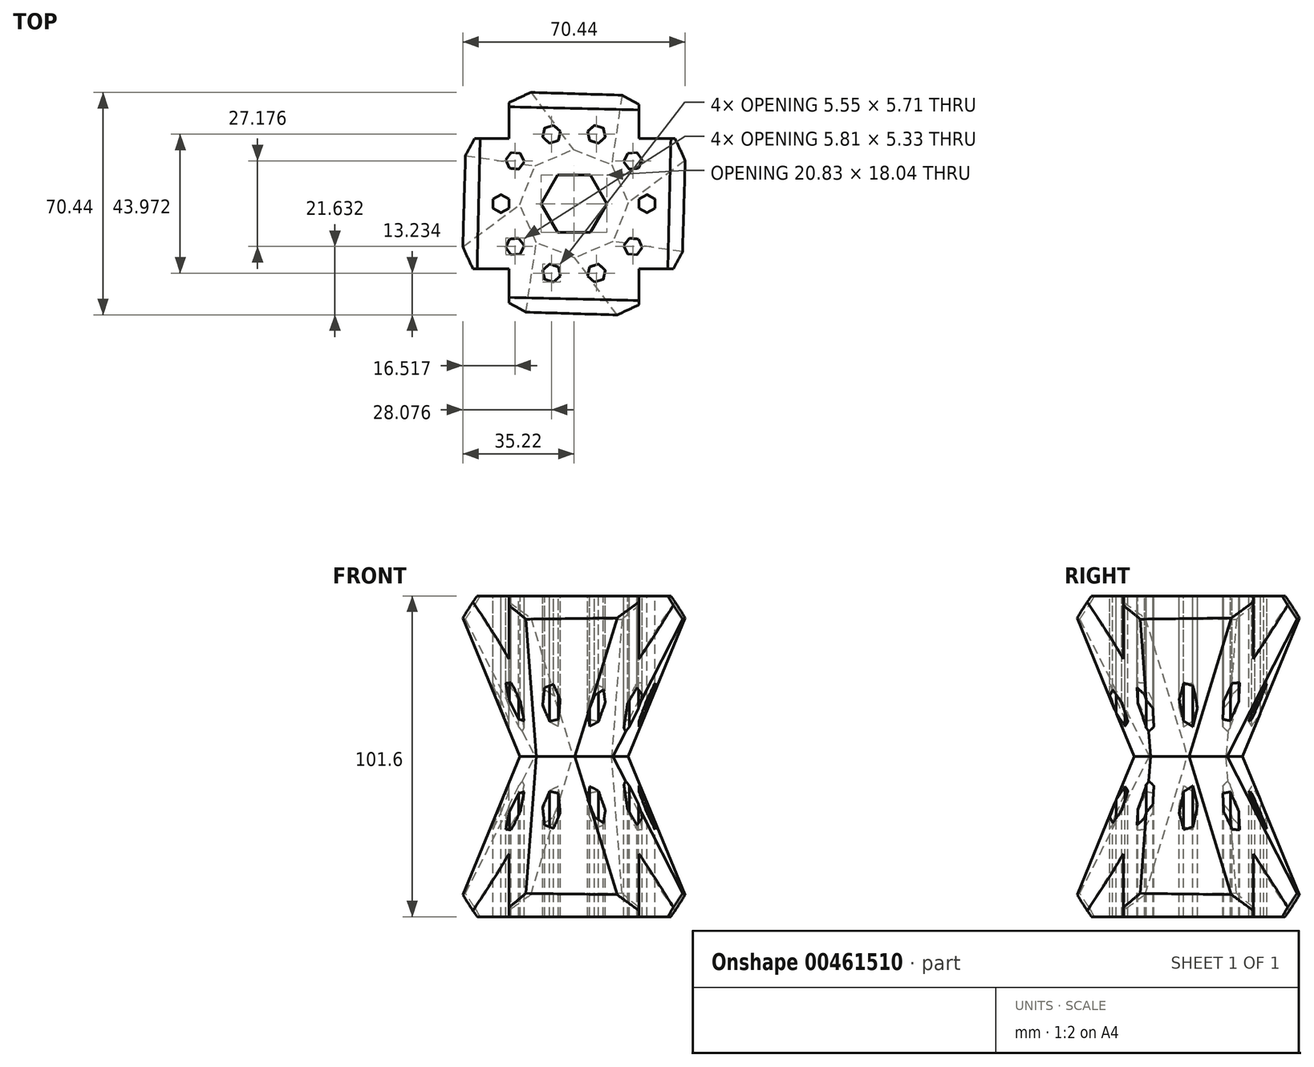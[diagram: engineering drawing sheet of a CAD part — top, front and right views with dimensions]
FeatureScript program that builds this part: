
annotation { "Feature Type Name" : "Feature", "Feature Type Description" : "" }
export const myFeature = defineFeature(function(context is Context, id is Id, definition is map)
    precondition{}
    {
        {
            var Q0;
            Q0=qCreatedBy(makeId("Top.planeOp"),FACE);
            var sketch = newSketch(context, id + "F0", { "sketchPlane" : qUnion([Q0])});
            skLineSegment(sketch, "E0", {"start": v(-123.7, 48.81) * mm, "end": v(88.1, 48.81) * mm, "construction": true});
            skCircle(sketch, "E1.cCircle", {"center": v(0, 0) * mm, "radius": 38.1 * mm, "construction": true});
            skLineSegment(sketch, "E1.0", {"start": v(15.78, 38.1) * mm, "end": v(38.1, 15.78) * mm});
            skLineSegment(sketch, "E1.1", {"start": v(38.1, 15.78) * mm, "end": v(38.1, -15.78) * mm});
            skLineSegment(sketch, "E1.2", {"start": v(38.1, -15.78) * mm, "end": v(15.78, -38.1) * mm});
            skLineSegment(sketch, "E1.3", {"start": v(15.78, -38.1) * mm, "end": v(-15.78, -38.1) * mm});
            skLineSegment(sketch, "E1.4", {"start": v(-15.78, -38.1) * mm, "end": v(-38.1, -15.78) * mm});
            skLineSegment(sketch, "E1.5", {"start": v(-38.1, -15.78) * mm, "end": v(-38.1, 15.78) * mm});
            skLineSegment(sketch, "E1.6", {"start": v(-38.1, 15.78) * mm, "end": v(-15.78, 38.1) * mm});
            skLineSegment(sketch, "E1.7", {"start": v(-15.78, 38.1) * mm, "end": v(15.78, 38.1) * mm});
            skPoint(sketch, "E1.0.midPoint", {"position": v(26.94, 26.94) * mm});
            skSolve(sketch);
        }
        {
            var Q0;
            Q0=qCreatedBy(makeId("Top.planeOp"),FACE);
            cPlane(context, id + "F1", {"entities" : qUnion([Q0]), "cplaneType" : CPlaneType.OFFSET, "offset" : 50.8 * mm, "width" : 152.4 * mm, "height" : 152.4 * mm});
        }
        {
            var Q0;
            Q0=qCreatedBy(id+"F1.planeOp",FACE);
            var sketch = newSketch(context, id + "F2", { "sketchPlane" : qUnion([Q0])});
            skCircle(sketch, "E2.cCircle", {"center": v(0, 0) * mm, "radius": 15.88 * mm, "construction": true});
            skLineSegment(sketch, "E2.0", {"start": v(0.3, -17.18) * mm, "end": v(-11.94, -12.36) * mm});
            skLineSegment(sketch, "E2.1", {"start": v(-11.94, -12.36) * mm, "end": v(-17.18, -0.3) * mm});
            skLineSegment(sketch, "E2.2", {"start": v(-17.18, -0.3) * mm, "end": v(-12.36, 11.94) * mm});
            skLineSegment(sketch, "E2.3", {"start": v(-12.36, 11.94) * mm, "end": v(-0.3, 17.18) * mm});
            skLineSegment(sketch, "E2.4", {"start": v(-0.3, 17.18) * mm, "end": v(11.94, 12.36) * mm});
            skLineSegment(sketch, "E2.5", {"start": v(11.94, 12.36) * mm, "end": v(17.18, 0.3) * mm});
            skLineSegment(sketch, "E2.6", {"start": v(17.18, 0.3) * mm, "end": v(12.36, -11.94) * mm});
            skLineSegment(sketch, "E2.7", {"start": v(12.36, -11.94) * mm, "end": v(0.3, -17.18) * mm});
            skPoint(sketch, "E2.0.midPoint", {"position": v(-5.82, -14.77) * mm});
            skSolve(sketch);
        }
        {
            var Q0;
            Q0=makeQuery(id+"F0.imprint","IMPRINT",FACE,{"disambiguationData":[TD([[makeQuery(id+"F0.imprint","IMPRINT",EDGE,{"derivedFrom":sQuery(id+"F0.wireOp",EDGE,"E1.0")}),-1.0]])]});
            var Q1;
            Q1=makeQuery(id+"F2.imprint","IMPRINT",FACE,{"disambiguationData":[TD([[makeQuery(id+"F2.imprint","IMPRINT",EDGE,{"derivedFrom":sQuery(id+"F2.wireOp",EDGE,"E2.0")}),-1.0]])]});
            loft(context, id + "F3", {"sheetProfilesArray" : [{ "sheetProfileEntities" : qUnion([Q0]) }, { "sheetProfileEntities" : qUnion([Q1]) }]});
        }
        {
            var Q0;
            Q0=makeQuery(id+"F3.opLoft","SWEPT_BODY",BODY,{"disambiguationData":[OSD([makeQuery(id+"F0.imprint","IMPRINT",FACE,{"disambiguationData":[TD([[makeQuery(id+"F0.imprint","IMPRINT",EDGE,{"derivedFrom":sQuery(id+"F0.wireOp",EDGE,"E1.0")}),-1.0]])]}),makeQuery(id+"F2.imprint","IMPRINT",FACE,{"disambiguationData":[TD([[makeQuery(id+"F2.imprint","IMPRINT",EDGE,{"derivedFrom":sQuery(id+"F2.wireOp",EDGE,"E2.0")}),-1.0]])]})])]});
            var Q1;
            Q1=qCreatedBy(id+"F1.planeOp",FACE);
            mirror(context, id + "F4", {"operationType" : NewBodyOperationType.ADD, "entities" : qUnion([Q0]), "mirrorPlane" : qUnion([Q1])});
        }
        {
            var Q0;
            Q0=makeQuery(id+"F4.opPattern","COPY",FACE,{"derivedFrom":makeQuery(id+"F3.opLoft","CAP_FACE",FACE,{"disambiguationData":[OSD([makeQuery(id+"F0.imprint","IMPRINT",FACE,{"disambiguationData":[TD([[makeQuery(id+"F0.imprint","IMPRINT",EDGE,{"derivedFrom":sQuery(id+"F0.wireOp",EDGE,"E1.0")}),-1.0]])]})])],"isStart":true}),"instanceName":"1"});
            var sketch = newSketch(context, id + "F5", { "sketchPlane" : qUnion([Q0])});
            skLineSegment(sketch, "E3", {"start": v(0, -25.16) * mm, "end": v(0, 28.29) * mm, "construction": true});
            skCircle(sketch, "E4.cCircle", {"center": v(0, 0) * mm, "radius": 9.02 * mm, "construction": true});
            skLineSegment(sketch, "E4.0", {"start": v(-10.41, 0) * mm, "end": v(-5.2, 9.02) * mm});
            skLineSegment(sketch, "E4.1", {"start": v(-5.2, 9.02) * mm, "end": v(5.2, 9.02) * mm});
            skLineSegment(sketch, "E4.2", {"start": v(5.2, 9.02) * mm, "end": v(10.41, 0) * mm});
            skLineSegment(sketch, "E4.3", {"start": v(10.41, 0) * mm, "end": v(5.2, -9.02) * mm});
            skLineSegment(sketch, "E4.4", {"start": v(5.2, -9.02) * mm, "end": v(-5.2, -9.02) * mm});
            skLineSegment(sketch, "E4.5", {"start": v(-5.2, -9.02) * mm, "end": v(-10.41, 0) * mm});
            skPoint(sketch, "E4.0.midPoint", {"position": v(-7.81, 4.5) * mm});
            skSolve(sketch);
        }
        {
            var Q0;
            Q0=makeQuery(id+"F5.imprint","IMPRINT",FACE,{"disambiguationData":[TD([[makeQuery(id+"F5.imprint","IMPRINT",EDGE,{"derivedFrom":sQuery(id+"F5.wireOp",EDGE,"E4.0")}),-1.0]])]});
            extrude(context, id + "F6", {"entities" : qUnion([Q0]), "operationType" : NewBodyOperationType.REMOVE, "endBound" : BoundingType.THROUGH_ALL, "oppositeDirection" : true, "depth" : 25.4 * mm});
        }
        {
            var Q0;
            Q0=makeQuery(id+"F4.opPattern","COPY",FACE,{"derivedFrom":makeQuery(id+"F3.opLoft","CAP_FACE",FACE,{"disambiguationData":[OSD([makeQuery(id+"F0.imprint","IMPRINT",FACE,{"disambiguationData":[TD([[makeQuery(id+"F0.imprint","IMPRINT",EDGE,{"derivedFrom":sQuery(id+"F0.wireOp",EDGE,"E1.0")}),-1.0]])]})])],"isStart":true}),"instanceName":"1"});
            var sketch = newSketch(context, id + "F7", { "sketchPlane" : qUnion([Q0])});
            skLineSegment(sketch, "E5", {"start": v(20.6, -33.3) * mm, "end": v(20.6, -20.6) * mm});
            skLineSegment(sketch, "E6", {"start": v(20.6, -20.6) * mm, "end": v(33.3, -20.6) * mm});
            skLineSegment(sketch, "E7", {"start": v(20.6, -20.6) * mm, "end": v(26.94, -26.94) * mm, "construction": true});
            skLineSegment(sketch, "E8.0", {"start": v(15.78, -38.1) * mm, "end": v(38.1, -15.78) * mm, "construction": true});
            skLineSegment(sketch, "E9", {"start": v(33.3, -20.6) * mm, "end": v(20.6, -33.3) * mm});
            skLineSegment(sketch, "E10.1.0", {"start": v(33.3, 20.6) * mm, "end": v(20.6, 20.6) * mm});
            skLineSegment(sketch, "E10.1.1", {"start": v(20.6, 20.6) * mm, "end": v(20.6, 33.3) * mm});
            skLineSegment(sketch, "E10.1.2", {"start": v(38.1, 15.78) * mm, "end": v(15.78, 38.1) * mm, "construction": true});
            skLineSegment(sketch, "E10.2.0", {"start": v(-20.6, 33.3) * mm, "end": v(-20.6, 20.6) * mm});
            skLineSegment(sketch, "E10.2.1", {"start": v(-20.6, 20.6) * mm, "end": v(-33.3, 20.6) * mm});
            skLineSegment(sketch, "E10.2.2", {"start": v(-15.78, 38.1) * mm, "end": v(-38.1, 15.78) * mm, "construction": true});
            skLineSegment(sketch, "E10.3.0", {"start": v(-33.3, -20.6) * mm, "end": v(-20.6, -20.6) * mm});
            skLineSegment(sketch, "E10.3.1", {"start": v(-20.6, -20.6) * mm, "end": v(-20.6, -33.3) * mm});
            skLineSegment(sketch, "E10.3.2", {"start": v(-38.1, -15.78) * mm, "end": v(-15.78, -38.1) * mm, "construction": true});
            skPoint(sketch, "E10.center", {"position": v(0, 0) * mm});
            skSolve(sketch);
        }
        {
            var Q0;
            Q0 = qSketchRegion(id + "F7", true);
            var Q1;
            {var subQ0=sQuery(id+"F7.wireOp",EDGE,"E10.1.0");Q1=makeQuery(id+"F7.imprint","IMPRINT",FACE,{"disambiguationData":[TD([[makeQuery(id+"F7.imprint","IMPRINT",EDGE,{"derivedFrom":subQ0}),-1.0]])]});}
            var Q2;
            {var subQ0=sQuery(id+"F7.wireOp",EDGE,"E10.2.0");Q2=makeQuery(id+"F7.imprint","IMPRINT",FACE,{"disambiguationData":[TD([[makeQuery(id+"F7.imprint","IMPRINT",EDGE,{"derivedFrom":subQ0}),-1.0]])]});}
            var Q3;
            {var subQ0=sQuery(id+"F7.wireOp",EDGE,"E10.3.0");Q3=makeQuery(id+"F7.imprint","IMPRINT",FACE,{"disambiguationData":[TD([[makeQuery(id+"F7.imprint","IMPRINT",EDGE,{"derivedFrom":subQ0}),-1.0]])]});}
            extrude(context, id + "F8", {"entities" : qUnion([Q0, Q1, Q2, Q3]), "operationType" : NewBodyOperationType.REMOVE, "endBound" : BoundingType.THROUGH_ALL, "oppositeDirection" : true, "depth" : 25.4 * mm});
        }
        {
            var Q0;
            Q0=makeQuery(id+"F4.opPattern","COPY",EDGE,{"derivedFrom":makeQuery(id+"F3.opLoft","MID_CAP_EDGE",EDGE,{"disambiguationData":[OSD([sQuery(id+"F0.wireOp",EDGE,"E1.0"),sQuery(id+"F0.wireOp",EDGE,"E1.1"),sQuery(id+"F0.wireOp",EDGE,"E1.2")])],"capPos":0.0}),"instanceName":"1"});
            var Q1;
            Q1=makeQuery(id+"F4.opPattern","COPY",EDGE,{"derivedFrom":makeQuery(id+"F3.opLoft","MID_CAP_EDGE",EDGE,{"disambiguationData":[OSD([sQuery(id+"F0.wireOp",EDGE,"E1.0"),sQuery(id+"F0.wireOp",EDGE,"E1.6"),sQuery(id+"F0.wireOp",EDGE,"E1.7")])],"capPos":0.0}),"instanceName":"1"});
            var Q2;
            Q2=makeQuery(id+"F4.opPattern","COPY",EDGE,{"derivedFrom":makeQuery(id+"F3.opLoft","MID_CAP_EDGE",EDGE,{"disambiguationData":[OSD([sQuery(id+"F0.wireOp",EDGE,"E1.4"),sQuery(id+"F0.wireOp",EDGE,"E1.5"),sQuery(id+"F0.wireOp",EDGE,"E1.6")])],"capPos":0.0}),"instanceName":"1"});
            var Q3;
            Q3=makeQuery(id+"F4.opPattern","COPY",EDGE,{"derivedFrom":makeQuery(id+"F3.opLoft","MID_CAP_EDGE",EDGE,{"disambiguationData":[OSD([sQuery(id+"F0.wireOp",EDGE,"E1.2"),sQuery(id+"F0.wireOp",EDGE,"E1.3"),sQuery(id+"F0.wireOp",EDGE,"E1.4")])],"capPos":0.0}),"instanceName":"1"});
            var Q4;
            Q4=makeQuery(id+"F3.opLoft","MID_CAP_EDGE",EDGE,{"disambiguationData":[OSD([sQuery(id+"F0.wireOp",EDGE,"E1.0"),sQuery(id+"F0.wireOp",EDGE,"E1.1"),sQuery(id+"F0.wireOp",EDGE,"E1.2")])],"capPos":0.0});
            var Q5;
            Q5=makeQuery(id+"F3.opLoft","MID_CAP_EDGE",EDGE,{"disambiguationData":[OSD([sQuery(id+"F0.wireOp",EDGE,"E1.0"),sQuery(id+"F0.wireOp",EDGE,"E1.6"),sQuery(id+"F0.wireOp",EDGE,"E1.7")])],"capPos":0.0});
            var Q6;
            Q6=makeQuery(id+"F3.opLoft","MID_CAP_EDGE",EDGE,{"disambiguationData":[OSD([sQuery(id+"F0.wireOp",EDGE,"E1.4"),sQuery(id+"F0.wireOp",EDGE,"E1.5"),sQuery(id+"F0.wireOp",EDGE,"E1.6")])],"capPos":0.0});
            var Q7;
            Q7=makeQuery(id+"F3.opLoft","MID_CAP_EDGE",EDGE,{"disambiguationData":[OSD([sQuery(id+"F0.wireOp",EDGE,"E1.2"),sQuery(id+"F0.wireOp",EDGE,"E1.3"),sQuery(id+"F0.wireOp",EDGE,"E1.4")])],"capPos":0.0});
            chamfer(context, id + "F9", {"entities" : qUnion([Q0, Q1, Q2, Q3, Q4, Q5, Q6, Q7]), "width" : 5.08 * mm, "tangentPropagation" : true});
        }
        {
            var Q0;
            Q0=makeQuery(id+"F4.opPattern","COPY",FACE,{"derivedFrom":makeQuery(id+"F3.opLoft","CAP_FACE",FACE,{"disambiguationData":[OSD([makeQuery(id+"F0.imprint","IMPRINT",FACE,{"disambiguationData":[TD([[makeQuery(id+"F0.imprint","IMPRINT",EDGE,{"derivedFrom":sQuery(id+"F0.wireOp",EDGE,"E1.0")}),-1.0]])]})])],"isStart":true}),"instanceName":"1"});
            var sketch = newSketch(context, id + "F10", { "sketchPlane" : qUnion([Q0])});
            skCircle(sketch, "E11.cCircle", {"center": v(23.12, 0) * mm, "radius": 2.53 * mm, "construction": true});
            skLineSegment(sketch, "E11.0", {"start": v(20.59, -1.46) * mm, "end": v(20.59, 1.46) * mm});
            skLineSegment(sketch, "E11.1", {"start": v(20.59, 1.46) * mm, "end": v(23.12, 2.92) * mm});
            skLineSegment(sketch, "E11.2", {"start": v(23.12, 2.92) * mm, "end": v(25.65, 1.46) * mm});
            skLineSegment(sketch, "E11.3", {"start": v(25.65, 1.46) * mm, "end": v(25.65, -1.46) * mm});
            skLineSegment(sketch, "E11.4", {"start": v(25.65, -1.46) * mm, "end": v(23.12, -2.92) * mm});
            skLineSegment(sketch, "E11.5", {"start": v(23.12, -2.92) * mm, "end": v(20.59, -1.46) * mm});
            skPoint(sketch, "E11.0.midPoint", {"position": v(20.59, 0) * mm});
            skCircle(sketch, "E12.1.0", {"center": v(18.7, 13.59) * mm, "radius": 2.53 * mm, "construction": true});
            skLineSegment(sketch, "E12.1.1", {"start": v(20.42, 11.23) * mm, "end": v(17.52, 10.92) * mm});
            skPoint(sketch, "E12.1.2", {"position": v(16.66, 12.1) * mm});
            skLineSegment(sketch, "E12.1.3", {"start": v(17.52, 10.92) * mm, "end": v(15.8, 13.28) * mm});
            skLineSegment(sketch, "E12.1.4", {"start": v(15.8, 13.28) * mm, "end": v(16.99, 15.95) * mm});
            skLineSegment(sketch, "E12.1.5", {"start": v(16.99, 15.95) * mm, "end": v(19.89, 16.25) * mm});
            skLineSegment(sketch, "E12.1.6", {"start": v(19.89, 16.25) * mm, "end": v(21.6, 13.9) * mm});
            skLineSegment(sketch, "E12.1.7", {"start": v(21.6, 13.9) * mm, "end": v(20.42, 11.23) * mm});
            skCircle(sketch, "E12.2.0", {"center": v(7.14, 21.99) * mm, "radius": 2.53 * mm, "construction": true});
            skLineSegment(sketch, "E12.2.1", {"start": v(9.92, 21.08) * mm, "end": v(7.75, 19.13) * mm});
            skPoint(sketch, "E12.2.2", {"position": v(6.36, 19.58) * mm});
            skLineSegment(sketch, "E12.2.3", {"start": v(7.75, 19.13) * mm, "end": v(4.97, 20.03) * mm});
            skLineSegment(sketch, "E12.2.4", {"start": v(4.97, 20.03) * mm, "end": v(4.37, 22.89) * mm});
            skLineSegment(sketch, "E12.2.5", {"start": v(4.37, 22.89) * mm, "end": v(6.54, 24.84) * mm});
            skLineSegment(sketch, "E12.2.6", {"start": v(6.54, 24.84) * mm, "end": v(9.31, 23.94) * mm});
            skLineSegment(sketch, "E12.2.7", {"start": v(9.31, 23.94) * mm, "end": v(9.92, 21.08) * mm});
            skCircle(sketch, "E12.3.0", {"center": v(-7.14, 21.99) * mm, "radius": 2.53 * mm, "construction": true});
            skLineSegment(sketch, "E12.3.1", {"start": v(-4.37, 22.89) * mm, "end": v(-4.97, 20.03) * mm});
            skPoint(sketch, "E12.3.2", {"position": v(-6.36, 19.58) * mm});
            skLineSegment(sketch, "E12.3.3", {"start": v(-4.97, 20.03) * mm, "end": v(-7.75, 19.13) * mm});
            skLineSegment(sketch, "E12.3.4", {"start": v(-7.75, 19.13) * mm, "end": v(-9.92, 21.08) * mm});
            skLineSegment(sketch, "E12.3.5", {"start": v(-9.92, 21.08) * mm, "end": v(-9.31, 23.94) * mm});
            skLineSegment(sketch, "E12.3.6", {"start": v(-9.31, 23.94) * mm, "end": v(-6.54, 24.84) * mm});
            skLineSegment(sketch, "E12.3.7", {"start": v(-6.54, 24.84) * mm, "end": v(-4.37, 22.89) * mm});
            skCircle(sketch, "E12.4.0", {"center": v(-18.7, 13.59) * mm, "radius": 2.53 * mm, "construction": true});
            skLineSegment(sketch, "E12.4.1", {"start": v(-16.99, 15.95) * mm, "end": v(-15.8, 13.28) * mm});
            skPoint(sketch, "E12.4.2", {"position": v(-16.66, 12.1) * mm});
            skLineSegment(sketch, "E12.4.3", {"start": v(-15.8, 13.28) * mm, "end": v(-17.52, 10.92) * mm});
            skLineSegment(sketch, "E12.4.4", {"start": v(-17.52, 10.92) * mm, "end": v(-20.42, 11.23) * mm});
            skLineSegment(sketch, "E12.4.5", {"start": v(-20.42, 11.23) * mm, "end": v(-21.6, 13.9) * mm});
            skLineSegment(sketch, "E12.4.6", {"start": v(-21.6, 13.9) * mm, "end": v(-19.89, 16.25) * mm});
            skLineSegment(sketch, "E12.4.7", {"start": v(-19.89, 16.25) * mm, "end": v(-16.99, 15.95) * mm});
            skCircle(sketch, "E12.5.0", {"center": v(-23.12, 0) * mm, "radius": 2.53 * mm, "construction": true});
            skLineSegment(sketch, "E12.5.1", {"start": v(-23.12, 2.92) * mm, "end": v(-20.59, 1.46) * mm});
            skPoint(sketch, "E12.5.2", {"position": v(-20.59, 0) * mm});
            skLineSegment(sketch, "E12.5.3", {"start": v(-20.59, 1.46) * mm, "end": v(-20.59, -1.46) * mm});
            skLineSegment(sketch, "E12.5.4", {"start": v(-20.59, -1.46) * mm, "end": v(-23.12, -2.92) * mm});
            skLineSegment(sketch, "E12.5.5", {"start": v(-23.12, -2.92) * mm, "end": v(-25.65, -1.46) * mm});
            skLineSegment(sketch, "E12.5.6", {"start": v(-25.65, -1.46) * mm, "end": v(-25.65, 1.46) * mm});
            skLineSegment(sketch, "E12.5.7", {"start": v(-25.65, 1.46) * mm, "end": v(-23.12, 2.92) * mm});
            skCircle(sketch, "E12.6.0", {"center": v(-18.7, -13.59) * mm, "radius": 2.53 * mm, "construction": true});
            skLineSegment(sketch, "E12.6.1", {"start": v(-20.42, -11.23) * mm, "end": v(-17.52, -10.92) * mm});
            skPoint(sketch, "E12.6.2", {"position": v(-16.66, -12.1) * mm});
            skLineSegment(sketch, "E12.6.3", {"start": v(-17.52, -10.92) * mm, "end": v(-15.8, -13.28) * mm});
            skLineSegment(sketch, "E12.6.4", {"start": v(-15.8, -13.28) * mm, "end": v(-16.99, -15.95) * mm});
            skLineSegment(sketch, "E12.6.5", {"start": v(-16.99, -15.95) * mm, "end": v(-19.89, -16.25) * mm});
            skLineSegment(sketch, "E12.6.6", {"start": v(-19.89, -16.25) * mm, "end": v(-21.6, -13.9) * mm});
            skLineSegment(sketch, "E12.6.7", {"start": v(-21.6, -13.9) * mm, "end": v(-20.42, -11.23) * mm});
            skCircle(sketch, "E12.7.0", {"center": v(-7.14, -21.99) * mm, "radius": 2.53 * mm, "construction": true});
            skLineSegment(sketch, "E12.7.1", {"start": v(-9.92, -21.08) * mm, "end": v(-7.75, -19.13) * mm});
            skPoint(sketch, "E12.7.2", {"position": v(-6.36, -19.58) * mm});
            skLineSegment(sketch, "E12.7.3", {"start": v(-7.75, -19.13) * mm, "end": v(-4.97, -20.03) * mm});
            skLineSegment(sketch, "E12.7.4", {"start": v(-4.97, -20.03) * mm, "end": v(-4.37, -22.89) * mm});
            skLineSegment(sketch, "E12.7.5", {"start": v(-4.37, -22.89) * mm, "end": v(-6.54, -24.84) * mm});
            skLineSegment(sketch, "E12.7.6", {"start": v(-6.54, -24.84) * mm, "end": v(-9.31, -23.94) * mm});
            skLineSegment(sketch, "E12.7.7", {"start": v(-9.31, -23.94) * mm, "end": v(-9.92, -21.08) * mm});
            skCircle(sketch, "E12.8.0", {"center": v(7.14, -21.99) * mm, "radius": 2.53 * mm, "construction": true});
            skLineSegment(sketch, "E12.8.1", {"start": v(4.37, -22.89) * mm, "end": v(4.97, -20.03) * mm});
            skPoint(sketch, "E12.8.2", {"position": v(6.36, -19.58) * mm});
            skLineSegment(sketch, "E12.8.3", {"start": v(4.97, -20.03) * mm, "end": v(7.75, -19.13) * mm});
            skLineSegment(sketch, "E12.8.4", {"start": v(7.75, -19.13) * mm, "end": v(9.92, -21.08) * mm});
            skLineSegment(sketch, "E12.8.5", {"start": v(9.92, -21.08) * mm, "end": v(9.31, -23.94) * mm});
            skLineSegment(sketch, "E12.8.6", {"start": v(9.31, -23.94) * mm, "end": v(6.54, -24.84) * mm});
            skLineSegment(sketch, "E12.8.7", {"start": v(6.54, -24.84) * mm, "end": v(4.37, -22.89) * mm});
            skCircle(sketch, "E12.9.0", {"center": v(18.7, -13.59) * mm, "radius": 2.53 * mm, "construction": true});
            skLineSegment(sketch, "E12.9.1", {"start": v(16.99, -15.95) * mm, "end": v(15.8, -13.28) * mm});
            skPoint(sketch, "E12.9.2", {"position": v(16.66, -12.1) * mm});
            skLineSegment(sketch, "E12.9.3", {"start": v(15.8, -13.28) * mm, "end": v(17.52, -10.92) * mm});
            skLineSegment(sketch, "E12.9.4", {"start": v(17.52, -10.92) * mm, "end": v(20.42, -11.23) * mm});
            skLineSegment(sketch, "E12.9.5", {"start": v(20.42, -11.23) * mm, "end": v(21.6, -13.9) * mm});
            skLineSegment(sketch, "E12.9.6", {"start": v(21.6, -13.9) * mm, "end": v(19.89, -16.25) * mm});
            skLineSegment(sketch, "E12.9.7", {"start": v(19.89, -16.25) * mm, "end": v(16.99, -15.95) * mm});
            skPoint(sketch, "E12.center", {"position": v(0, 0) * mm});
            skSolve(sketch);
        }
        {
            var Q0;
            Q0 = qSketchRegion(id + "F10", true);
            extrude(context, id + "F11", {"entities" : qUnion([Q0]), "operationType" : NewBodyOperationType.REMOVE, "endBound" : BoundingType.THROUGH_ALL, "oppositeDirection" : true, "depth" : 50.8 * mm});
        }
    });
